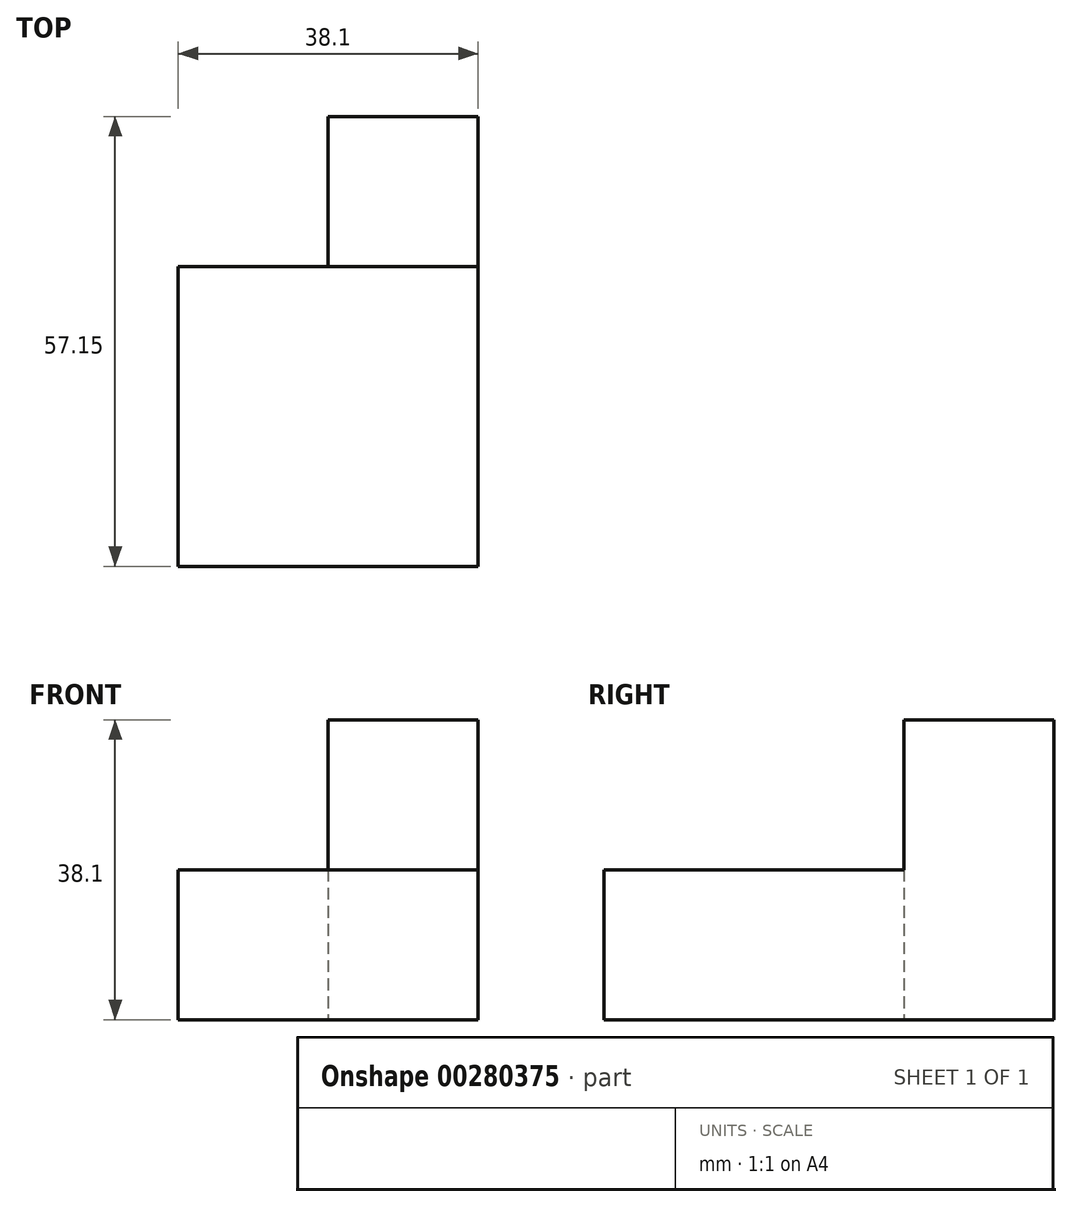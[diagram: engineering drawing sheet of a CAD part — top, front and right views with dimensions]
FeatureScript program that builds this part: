
annotation { "Feature Type Name" : "Feature", "Feature Type Description" : "" }
export const myFeature = defineFeature(function(context is Context, id is Id, definition is map)
    precondition{}
    {
        {
            var Q0;
            Q0=qCreatedBy(makeId("Top.planeOp"),FACE);
            var sketch = newSketch(context, id + "F0", { "sketchPlane" : qUnion([Q0])});
            skLineSegment(sketch, "E0.bottom", {"start": v(0, 0) * mm, "end": v(38.1, 0) * mm});
            skLineSegment(sketch, "E0.top", {"start": v(0, 38.1) * mm, "end": v(19.05, 38.1) * mm});
            skLineSegment(sketch, "E0.left", {"start": v(0, 0) * mm, "end": v(0, 38.1) * mm});
            skLineSegment(sketch, "E0.right", {"start": v(38.1, 0) * mm, "end": v(38.1, 38.1) * mm});
            skLineSegment(sketch, "E1", {"start": v(19.05, 38.1) * mm, "end": v(19.05, 57.15) * mm});
            skLineSegment(sketch, "E2", {"start": v(19.05, 57.15) * mm, "end": v(38.1, 57.15) * mm});
            skLineSegment(sketch, "E3", {"start": v(38.1, 57.15) * mm, "end": v(38.1, 38.1) * mm});
            skSolve(sketch);
        }
        {
            var Q0;
            Q0=makeQuery(id+"F0.imprint","IMPRINT",FACE,{"disambiguationData":[TD([[makeQuery(id+"F0.imprint","IMPRINT",EDGE,{"derivedFrom":sQuery(id+"F0.wireOp",EDGE,"E0.bottom")}),1.0]])]});
            extrude(context, id + "F1", {"entities" : qUnion([Q0]), "depth" : 19.05 * mm});
        }
        {
            var Q0;
            Q0=makeQuery(id+"F1.opExtrude","CAP_FACE",FACE,{"disambiguationData":[OSD([sQuery(id+"F0.wireOp",EDGE,"E0.bottom"),sQuery(id+"F0.wireOp",EDGE,"E0.top"),sQuery(id+"F0.wireOp",EDGE,"E0.left"),sQuery(id+"F0.wireOp",EDGE,"E0.right"),sQuery(id+"F0.wireOp",EDGE,"E1"),sQuery(id+"F0.wireOp",EDGE,"E2"),sQuery(id+"F0.wireOp",EDGE,"E3")])],"isStart":false});
            var sketch = newSketch(context, id + "F2", { "sketchPlane" : qUnion([Q0])});
            skLineSegment(sketch, "E4.bottom", {"start": v(19.05, 38.1) * mm, "end": v(38.1, 38.1) * mm});
            skLineSegment(sketch, "E4.top", {"start": v(19.05, 57.15) * mm, "end": v(38.1, 57.15) * mm});
            skLineSegment(sketch, "E4.left", {"start": v(19.05, 38.1) * mm, "end": v(19.05, 57.15) * mm});
            skLineSegment(sketch, "E4.right", {"start": v(38.1, 38.1) * mm, "end": v(38.1, 57.15) * mm});
            skSolve(sketch);
        }
        {
            var Q0;
            Q0 = qSketchRegion(id + "F2", true);
            extrude(context, id + "F3", {"entities" : qUnion([Q0]), "operationType" : NewBodyOperationType.ADD, "depth" : 19.05 * mm});
        }
    });
